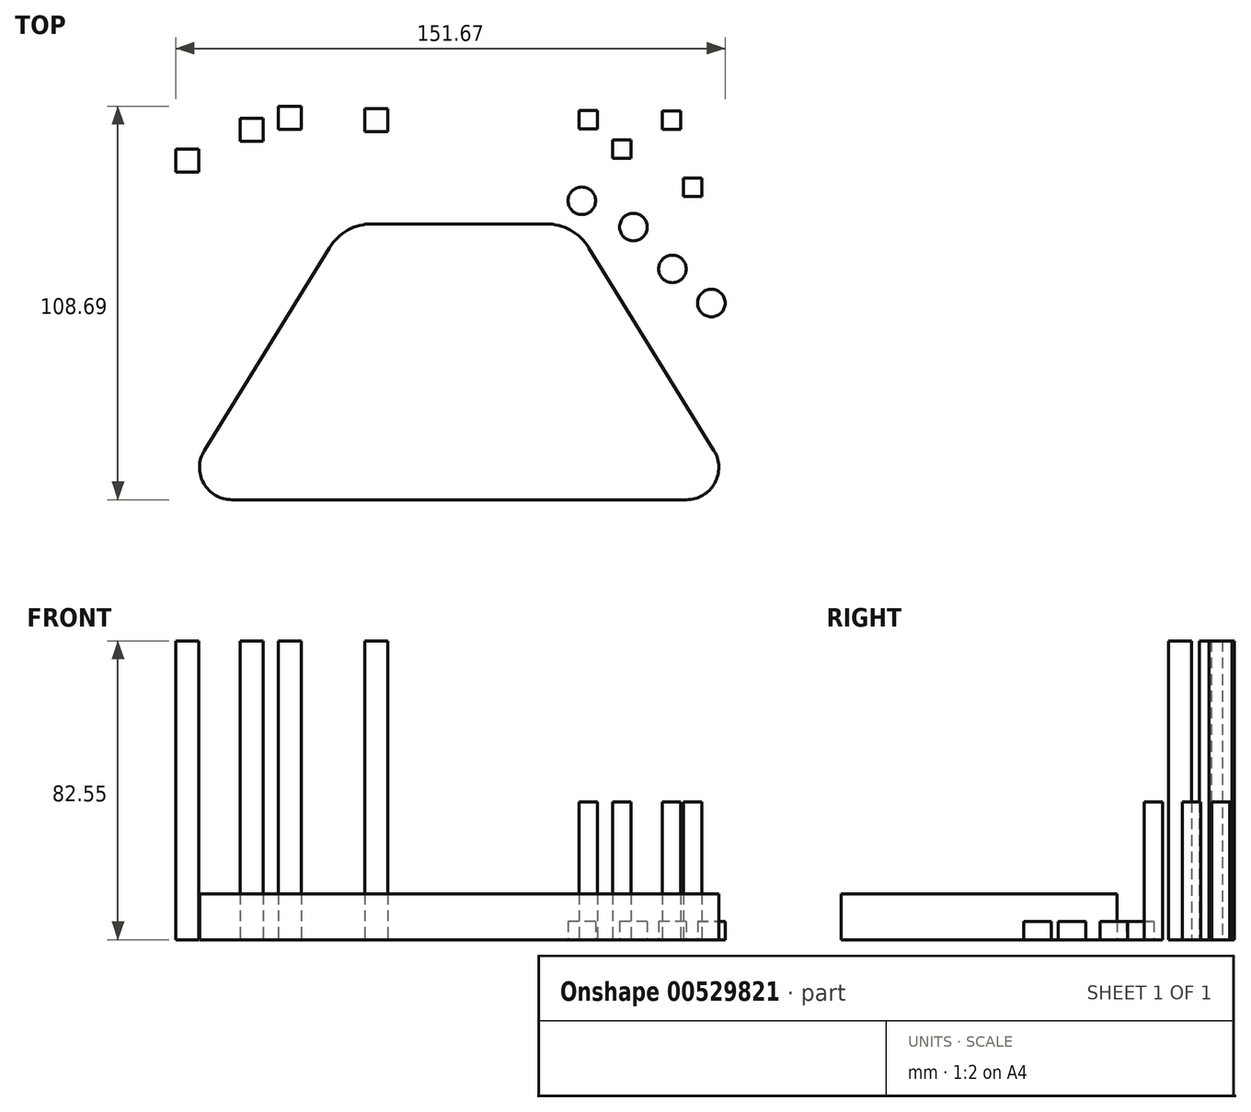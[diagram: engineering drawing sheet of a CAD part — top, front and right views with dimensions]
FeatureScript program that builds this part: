
annotation { "Feature Type Name" : "Feature", "Feature Type Description" : "" }
export const myFeature = defineFeature(function(context is Context, id is Id, definition is map)
    precondition{}
    {
        {
            var Q0;
            Q0=qCreatedBy(makeId("Top.planeOp"),FACE);
            var sketch = newSketch(context, id + "F0", { "sketchPlane" : qUnion([Q0])});
            skLineSegment(sketch, "E0.bottom", {"start": v(-23.13, 40.03) * mm, "end": v(24.77, 40.03) * mm});
            skLineSegment(sketch, "E0.top", {"start": v(-30.93, -36.17) * mm, "end": v(32.57, -36.17) * mm});
            skLineSegment(sketch, "E0.left", {"start": v(-30.93, 40.03) * mm, "end": v(-30.93, -36.17) * mm});
            skLineSegment(sketch, "E0.right", {"start": v(32.57, 40.03) * mm, "end": v(32.57, -36.17) * mm});
            skLineSegment(sketch, "E1", {"start": v(-30.93, -36.17) * mm, "end": v(-62, -36.17) * mm});
            skLineSegment(sketch, "E2", {"start": v(32.57, -36.17) * mm, "end": v(63.64, -36.17) * mm});
            skLineSegment(sketch, "E3", {"start": v(-69.56, -22.62) * mm, "end": v(-35.02, 33.4) * mm});
            skLineSegment(sketch, "E4", {"start": v(36.66, 33.4) * mm, "end": v(71.2, -22.62) * mm});
            skPoint(sketch, "E5.visualSharp", {"position": v(-30.93, 40.03) * mm});
            skArc(sketch, "E5.filletArc", {"start": v(-23.13, 40.03) * mm, "mid": v(-29.94, 38.26) * mm, "end": v(-35.02, 33.4) * mm});
            skPoint(sketch, "E6.visualSharp", {"position": v(32.57, 40.03) * mm});
            skArc(sketch, "E6.filletArc", {"start": v(36.66, 33.4) * mm, "mid": v(31.58, 38.26) * mm, "end": v(24.77, 40.03) * mm});
            skPoint(sketch, "E7.visualSharp", {"position": v(-77.92, -36.17) * mm});
            skArc(sketch, "E7.filletArc", {"start": v(-69.56, -22.62) * mm, "mid": v(-69.75, -31.62) * mm, "end": v(-62, -36.17) * mm});
            skPoint(sketch, "E8.visualSharp", {"position": v(79.56, -36.17) * mm});
            skArc(sketch, "E8.filletArc", {"start": v(63.64, -36.17) * mm, "mid": v(71.4, -31.62) * mm, "end": v(71.2, -22.62) * mm});
            skSolve(sketch);
        }
        {
            var Q0;
            Q0 = qSketchRegion(id + "F0", true);
            extrude(context, id + "F1", {"entities" : qUnion([Q0]), "depth" : 12.7 * mm, "offsetDistance" : 25.4 * mm});
        }
        {
            var Q0;
            Q0=qCreatedBy(makeId("Top.planeOp"),FACE);
            var sketch = newSketch(context, id + "F2", { "sketchPlane" : qUnion([Q0])});
            skLineSegment(sketch, "E9.bottom", {"start": v(-53.34, 62.8) * mm, "end": v(-59.7, 62.8) * mm});
            skLineSegment(sketch, "E9.top", {"start": v(-53.34, 69.15) * mm, "end": v(-59.7, 69.15) * mm});
            skLineSegment(sketch, "E9.left", {"start": v(-53.34, 62.8) * mm, "end": v(-53.34, 69.15) * mm});
            skLineSegment(sketch, "E9.right", {"start": v(-59.7, 62.8) * mm, "end": v(-59.7, 69.15) * mm});
            skPoint(sketch, "E9.middle", {"position": v(-56.52, 65.97) * mm});
            skLineSegment(sketch, "E10.bottom", {"start": v(-42.78, 66.17) * mm, "end": v(-49.13, 66.17) * mm});
            skLineSegment(sketch, "E10.top", {"start": v(-42.78, 72.52) * mm, "end": v(-49.13, 72.52) * mm});
            skLineSegment(sketch, "E10.left", {"start": v(-42.78, 66.17) * mm, "end": v(-42.78, 72.52) * mm});
            skLineSegment(sketch, "E10.right", {"start": v(-49.13, 66.17) * mm, "end": v(-49.13, 72.52) * mm});
            skPoint(sketch, "E10.middle", {"position": v(-45.96, 69.34) * mm});
            skLineSegment(sketch, "E11.bottom", {"start": v(-71.03, 54.3) * mm, "end": v(-77.38, 54.3) * mm});
            skLineSegment(sketch, "E11.top", {"start": v(-71.03, 60.65) * mm, "end": v(-77.38, 60.65) * mm});
            skLineSegment(sketch, "E11.left", {"start": v(-71.03, 54.3) * mm, "end": v(-71.03, 60.65) * mm});
            skLineSegment(sketch, "E11.right", {"start": v(-77.38, 54.3) * mm, "end": v(-77.38, 60.65) * mm});
            skPoint(sketch, "E11.middle", {"position": v(-74.2, 57.48) * mm});
            skLineSegment(sketch, "E12.bottom", {"start": v(-18.86, 65.54) * mm, "end": v(-25.21, 65.54) * mm});
            skLineSegment(sketch, "E12.top", {"start": v(-18.86, 71.89) * mm, "end": v(-25.21, 71.89) * mm});
            skLineSegment(sketch, "E12.left", {"start": v(-18.86, 65.54) * mm, "end": v(-18.86, 71.89) * mm});
            skLineSegment(sketch, "E12.right", {"start": v(-25.21, 65.54) * mm, "end": v(-25.21, 71.89) * mm});
            skPoint(sketch, "E12.middle", {"position": v(-22.04, 68.71) * mm});
            skSolve(sketch);
        }
        {
            var Q0;
            Q0 = qSketchRegion(id + "F2", true);
            extrude(context, id + "F3", {"entities" : qUnion([Q0]), "depth" : 82.55 * mm, "offsetDistance" : 25.4 * mm});
        }
        {
            var Q0;
            Q0=qCreatedBy(makeId("Top.planeOp"),FACE);
            var sketch = newSketch(context, id + "F4", { "sketchPlane" : qUnion([Q0])});
            skLineSegment(sketch, "E13.bottom", {"start": v(38.98, 66.3) * mm, "end": v(33.9, 66.3) * mm});
            skLineSegment(sketch, "E13.top", {"start": v(38.98, 71.37) * mm, "end": v(33.9, 71.37) * mm});
            skLineSegment(sketch, "E13.left", {"start": v(38.98, 66.3) * mm, "end": v(38.98, 71.37) * mm});
            skLineSegment(sketch, "E13.right", {"start": v(33.9, 66.3) * mm, "end": v(33.9, 71.37) * mm});
            skPoint(sketch, "E13.middle", {"position": v(36.44, 68.83) * mm});
            skLineSegment(sketch, "E14.bottom", {"start": v(62, 66.17) * mm, "end": v(56.91, 66.17) * mm});
            skLineSegment(sketch, "E14.top", {"start": v(62, 71.25) * mm, "end": v(56.91, 71.25) * mm});
            skLineSegment(sketch, "E14.left", {"start": v(62, 66.17) * mm, "end": v(62, 71.25) * mm});
            skLineSegment(sketch, "E14.right", {"start": v(56.91, 66.17) * mm, "end": v(56.91, 71.25) * mm});
            skPoint(sketch, "E14.middle", {"position": v(59.45, 68.71) * mm});
            skLineSegment(sketch, "E15.bottom", {"start": v(48.27, 58.1) * mm, "end": v(43.2, 58.1) * mm});
            skLineSegment(sketch, "E15.top", {"start": v(48.27, 63.19) * mm, "end": v(43.2, 63.19) * mm});
            skLineSegment(sketch, "E15.left", {"start": v(48.27, 58.1) * mm, "end": v(48.27, 63.19) * mm});
            skLineSegment(sketch, "E15.right", {"start": v(43.2, 58.1) * mm, "end": v(43.2, 63.19) * mm});
            skPoint(sketch, "E15.middle", {"position": v(45.73, 60.65) * mm});
            skLineSegment(sketch, "E16.bottom", {"start": v(67.9, 47.62) * mm, "end": v(62.83, 47.62) * mm});
            skLineSegment(sketch, "E16.top", {"start": v(67.9, 52.7) * mm, "end": v(62.83, 52.7) * mm});
            skLineSegment(sketch, "E16.left", {"start": v(67.9, 47.62) * mm, "end": v(67.9, 52.7) * mm});
            skLineSegment(sketch, "E16.right", {"start": v(62.83, 47.62) * mm, "end": v(62.83, 52.7) * mm});
            skPoint(sketch, "E16.middle", {"position": v(65.37, 50.16) * mm});
            skSolve(sketch);
        }
        {
            var Q0;
            Q0 = qSketchRegion(id + "F4", true);
            extrude(context, id + "F5", {"entities" : qUnion([Q0]), "depth" : 38.1 * mm, "offsetDistance" : 25.4 * mm});
        }
        {
            var Q0;
            Q0=qCreatedBy(makeId("Top.planeOp"),FACE);
            var sketch = newSketch(context, id + "F6", { "sketchPlane" : qUnion([Q0])});
            skCircle(sketch, "E17", {"center": v(59.72, 27.57) * mm, "radius": 3.81 * mm});
            skCircle(sketch, "E18", {"center": v(70.48, 18.15) * mm, "radius": 3.81 * mm});
            skCircle(sketch, "E19", {"center": v(48.96, 39.13) * mm, "radius": 3.81 * mm});
            skCircle(sketch, "E20", {"center": v(34.7, 46.4) * mm, "radius": 3.81 * mm});
            skSolve(sketch);
        }
        {
            var Q0;
            Q0=makeQuery(id+"F6.imprint","IMPRINT",FACE,{"disambiguationData":[TD([[makeQuery(id+"F6.imprint","IMPRINT",EDGE,{"derivedFrom":sQuery(id+"F6.wireOp",EDGE,"E20")}),1.0]])]});
            var Q1;
            Q1=makeQuery(id+"F6.imprint","IMPRINT",FACE,{"disambiguationData":[TD([[makeQuery(id+"F6.imprint","IMPRINT",EDGE,{"derivedFrom":sQuery(id+"F6.wireOp",EDGE,"E19")}),1.0]])]});
            var Q2;
            Q2=makeQuery(id+"F6.imprint","IMPRINT",FACE,{"disambiguationData":[TD([[makeQuery(id+"F6.imprint","IMPRINT",EDGE,{"derivedFrom":sQuery(id+"F6.wireOp",EDGE,"E17")}),1.0]])]});
            var Q3;
            Q3=makeQuery(id+"F6.imprint","IMPRINT",FACE,{"disambiguationData":[TD([[makeQuery(id+"F6.imprint","IMPRINT",EDGE,{"derivedFrom":sQuery(id+"F6.wireOp",EDGE,"E18")}),1.0]])]});
            extrude(context, id + "F7", {"entities" : qUnion([Q0, Q1, Q2, Q3]), "depth" : 5.08 * mm, "offsetDistance" : 25.4 * mm});
        }
    });
